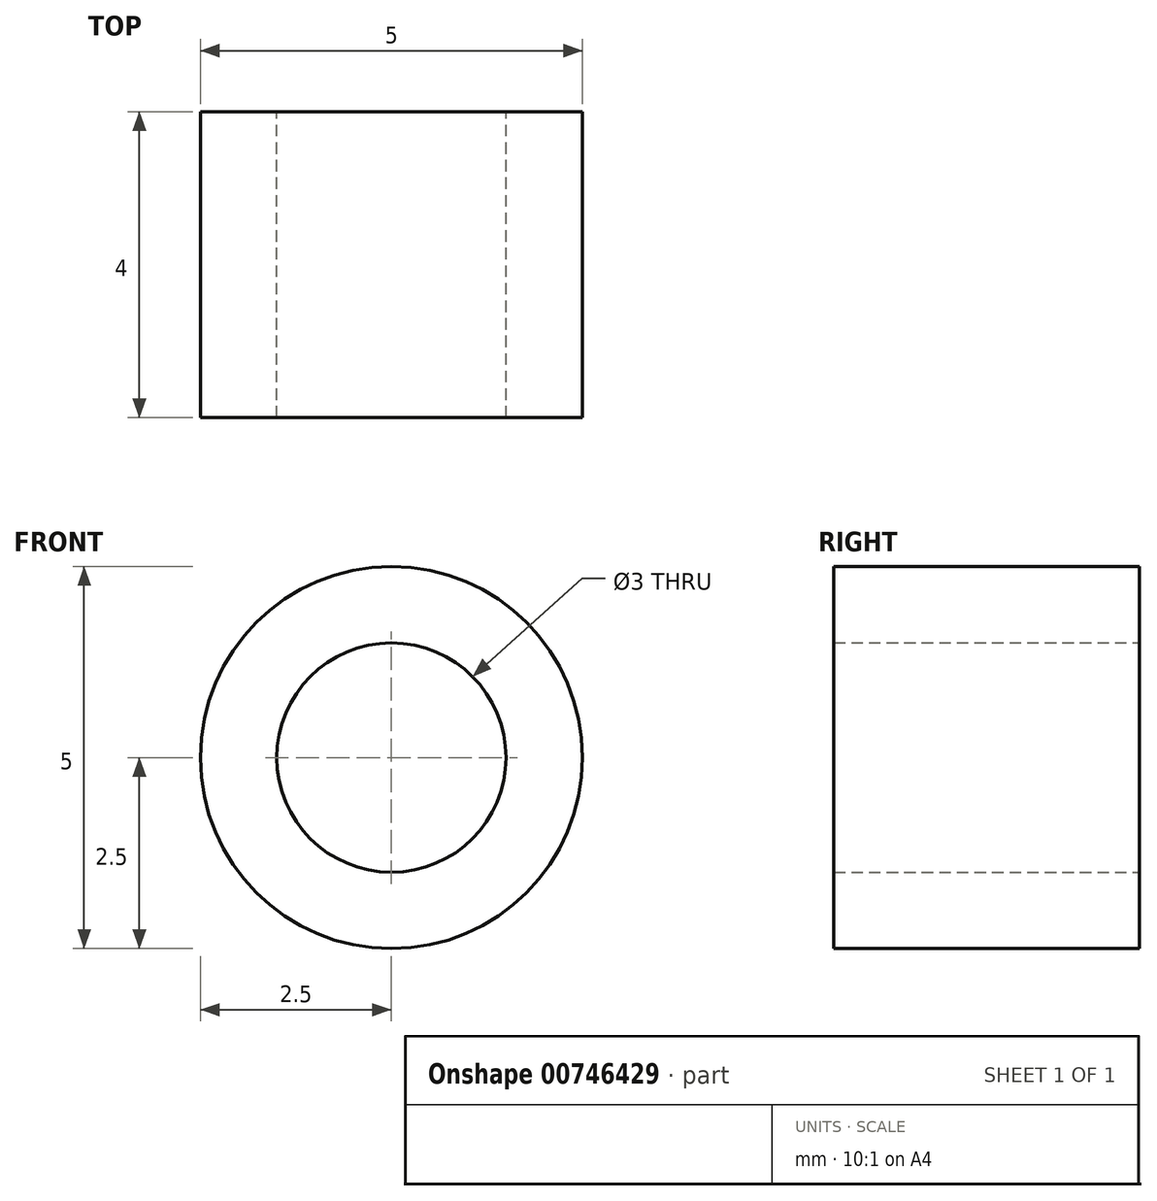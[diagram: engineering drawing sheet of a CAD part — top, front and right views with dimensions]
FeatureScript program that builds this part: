
annotation { "Feature Type Name" : "Feature", "Feature Type Description" : "" }
export const myFeature = defineFeature(function(context is Context, id is Id, definition is map)
    precondition{}
    {
        {
            var Q0;
            Q0=qCreatedBy(makeId("Top.planeOp"),FACE);
            var sketch = newSketch(context, id + "F0", { "sketchPlane" : qUnion([Q0])});
            skCircle(sketch, "E0", {"center": v(0, 0) * mm, "radius": 1.5 * mm});
            skCircle(sketch, "E1", {"center": v(0, 0) * mm, "radius": 2.5 * mm});
            skSolve(sketch);
        }
        {
            var Q0;
            Q0 = qSketchRegion(id + "F0", true);
            extrude(context, id + "F1", {"entities" : qUnion([Q0]), "depth" : 4 * mm, "offsetDistance" : 25.4 * mm});
        }
        {
            var Q0;
            Q0=qCreatedBy(makeId("Top.planeOp"),FACE);
            var sketch = newSketch(context, id + "F2", { "sketchPlane" : qUnion([Q0])});
            skLineSegment(sketch, "E2", {"start": v(-22.1, 0) * mm, "end": v(21.98, 0) * mm});
            skSolve(sketch);
        }
        {
            var Q0;
            Q0=makeQuery(id+"F1.opExtrude","SWEPT_BODY",BODY,{"disambiguationData":[OSD([sQuery(id+"F0.wireOp",EDGE,"E0"),sQuery(id+"F0.wireOp",EDGE,"E1")])]});
            var Q1;
            Q1=sQuery(id+"F2.wireOp",EDGE,"E2");
            transform(context, id + "F3", {"entities" : qUnion([Q0]), "transformType" : TransformType.ROTATION, "transformAxis" : qUnion([Q1]), "angle" : 90 * degree, "makeCopy" : false});
        }
    });
